# Revit family: HR400
name_source: partatom
category: Apparecchi idraulici
units: mm (PartAtom-declared; Revit-internal decimal feet)

## family parameters
Basato su piano di lavoro = No
Condiviso = No
Mantieni orientamento annotazione = No
Numero OmniClass = 23.45.55.17
Punto di calcolo locali = No
Quota connettore circolare = Usa diametro
Sempre verticale = Sì
Taglio con vuoti quando caricato = No
Tipo di parte = Normale
Titolo OmniClass = Mixing Faucets

## types (8) — shared parameters
Cold water inlet = 10 mm  [stored 0.0328084 ft]
Commenti sul tipo = Two holes wall mounted shower
Connessione CW = No
Connessione HW = No
Connessione di scarico = No
Connessione di ventilazione = No
Descrizione = Two holes wall mounted shower
Hot water inlet = 10 mm  [stored 0.0328084 ft]
Produttore = IB Rubinetterie S.p.A.
URL = https://www.weareib.it
zero-valued in all types: Prospetto di default

## per-type parameters (varying)
| type | Finishes surface | Immagine tipo | Modello |
| Chrome | IB_Chrome | HR400CC.jpg | HR400CC |
| Brushed nickel | IB_Brushed nickel | HR400SS.jpg | HR400SS |
| Antique Bronze | IB_Antique bronze | HR400BB.jpg | HR400BB |
| Pale gold | IB_Pale gold | HR400II.jpg | HR400II |
| Brushed gold | IB_brushed gold | HR400OS.jpg | HR400OS |
| Platinum | IB_Platinum | HR400PL.jpg | HR400PL |
| Rose gold | IB_Rose gold | HR400RS.jpg | HR400RS |
| Antique Copper | IB_Antique copper | HR400RR.jpg | HR400RR |

note: [stored X ft] marks values corroborated as IEEE doubles in the binary element streams (Revit-internal decimal feet)
